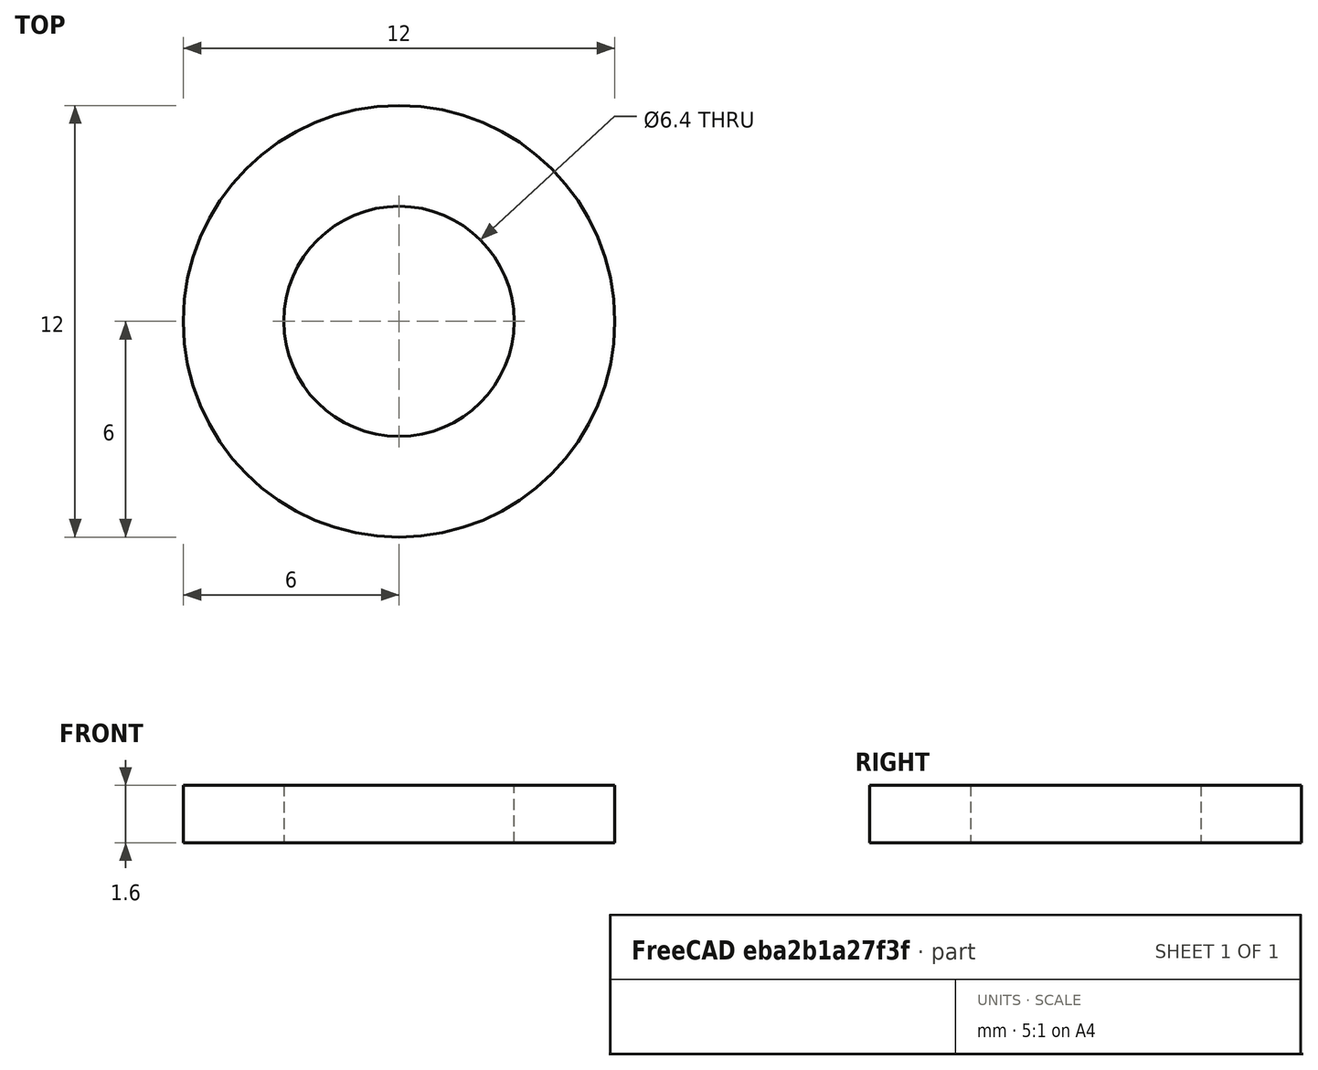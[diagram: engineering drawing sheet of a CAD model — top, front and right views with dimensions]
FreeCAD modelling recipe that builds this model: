
FCSTD DOCUMENT  (FreeCAD 0.19R24276 (Git))
Label: WASHER-M6
License: All rights reserved
LicenseURL: http://en.wikipedia.org/wiki/All_rights_reserved
objects: PartDesign::CoordinateSystem×2, Sketcher::SketchObject×1, PartDesign::Pad×1, PartDesign::Body×1
note: 6 computed .brp shape members not serialized (recipe doc carries the construction recipe); baked Part::Feature solids carry a one-line shape summary decoded from their .brp

FEATURE [PartDesign::CoordinateSystem] LCS_0
  AttacherType = Attacher::AttachEngine3D
  MapMode = 2
  Support = -> [X_Axis]
FEATURE [Sketcher::SketchObject] Sketch
  FullyConstrained = false
  MapMode = 5
  Support = -> [XY_Plane]
  sketch-geometry (2):
    g0: Circle CenterX=0 CenterY=0 CenterZ=0 NormalX=0 NormalY=0 NormalZ=1 AngleXU=0 Radius=3.2
    g1: Circle CenterX=0 CenterY=0 CenterZ=0 NormalX=0 NormalY=0 NormalZ=1 AngleXU=0 Radius=6
  constraints (4):
    c: Coincident(g0,g-1)
    c: Coincident(g1,g0)
    c: Diameter(g1) = 12
    c: Diameter(g0) = 6.4
FEATURE [PartDesign::Pad] Pad
  Direction = (1,1,1)
  Length = 1.6
  Length2 = 100
  Profile = -> Sketch
  Refine = true
  Type = 0
FEATURE [PartDesign::CoordinateSystem] LCS_1
  AttacherType = Attacher::AttachEngine3D
  MapMode = 11
  Placement = pos=(-4e-16,0,1.6) rot=(0,0,1;1.5708rad)
  Support = -> [Pad]
FEATURE [PartDesign::Body] WASHER_M6
  Group = -> [LCS_0,Sketch,Pad,LCS_1]
  Origin = -> Origin
  Tip = -> Pad
